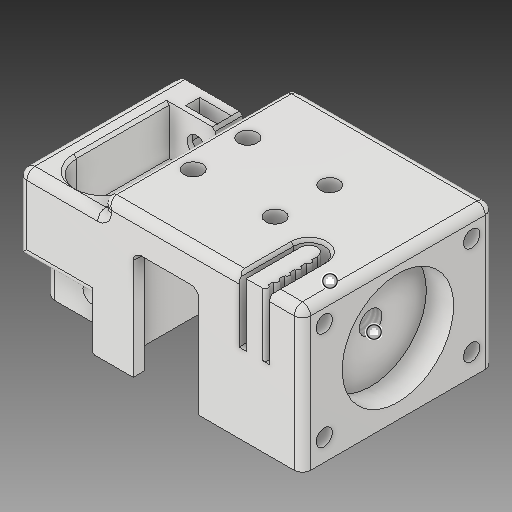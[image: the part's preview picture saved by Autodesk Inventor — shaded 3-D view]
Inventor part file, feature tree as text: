
AUTODESK INVENTOR PART (.ipt)
format: ipt  version: 2019 (Build 230136000, 136)  size: 547,840 bytes
history: native  units: mm
features: sketch x19, extrude x18, fillet x3, pattern_linear x2, plane x2, thicken_offset x2, mirror x1, chamfer x1, hole x1
ambient origin geometry x8: Origin, YZ Plane, XZ Plane, XY Plane, X Axis, Y Axis, Z Axis, Center Point
bodies: Solid1 (feature_tree)
feature tree (49):
  extrude  "Extrusion1"  Depth=15.0mm
  extrude  "Extrusion2"  Depth=20.0mm
  extrude  "Extrusion15"  Depth=15.0mm
  extrude  "Extrusion16"  Depth=10.0mm
  extrude  "Extrusion21"  Depth=10.0mm
  extrude  "Extrusion22"  Depth=10.0mm
  mirror  "Mirror12"
  extrude  "Extrusion23"  Depth=11.5mm TaperAngle=0.0deg
  pattern_linear  "Rectangular Pattern4"  Count1=5 Spacing1=2.0mm
  extrude  "Extrusion24"  Depth=3.0mm
  extrude  "Extrusion25"  Depth=10.0mm
  pattern_linear  "Rectangular Pattern5"  Spacing1=1.0mm  [1 undecoded]
  extrude  "Extrusion26"  Depth=10.0mm TaperAngle=0.0deg
  extrude  "Extrusion27"  Depth=2.0mm
  plane  "Work Plane6"
  extrude  "Extrusion28"  Depth=2.0mm
  thicken_offset  "Thicken1"
  extrude  "Extrusion29"  Depth=2.0mm
  extrude  "Extrusion30"  Depth=10.0mm
  extrude  "Extrusion31"  Depth=2.0mm
  plane  "Work Plane7"
  extrude  "Extrusion32"  Depth=2.0mm
  extrude  "Extrusion33"  Depth=2.0mm TaperAngle=0.0deg
  extrude  "Extrusion34"  Depth=2.0mm
  chamfer  "Chamfer5"  Distance=10.0mm
  thicken_offset  "Thicken2"
  fillet  "Fillet2"  [1 undecoded]
  fillet  "Fillet3"  Radius=2.6mm
  fillet  "Fillet4"  Radius=5.8mm
  hole  "Hole1"  [1 undecoded]
  sketch  "Sketch1"  dims[d0=3.0mm d1=15.0mm]
  sketch  "Sketch2"  dims[d2=20.0mm d4=23.0mm]
  sketch  "Sketch18"  dims[d5=35.0mm d6=0.0mm d7=15.0mm]
  sketch  "Sketch19"  dims[d8=10.0mm d9=3.4mm]
  sketch  "Sketch24"  dims[d10=10.0mm d11=0.0mm d106=1.3mm]
  sketch  "Sketch26"  dims[d107=10.0mm d108=3.0mm]
  sketch  "Sketch27"  dims[d110=3.4mm d111=11.5mm d112=0.0mm]
  sketch  "Sketch28"  dims[d113=13.5mm]
  sketch  "Sketch29"  dims[d114=6.0mm]
  sketch  "Sketch30"  dims[d115=12.0mm d116=0.0mm]
  sketch  "Sketch31"  dims[d140=3.0mm d141=0.0mm]
  sketch  "Sketch32"  dims[d142=12.0mm]
  sketch  "Sketch33"  dims[d143=3.0mm]
  sketch  "Sketch34"  dims[d144=2.0mm d145=0.0mm]
  sketch  "Sketch35"  dims[d146=1.0mm]
  sketch  "Sketch36"  dims[d147=2.0mm d148=0.0mm d149=50.0mm d151=2.0mm]
  sketch  "Sketch37"  dims[d152=1.3mm d153=3.0mm]
  sketch  "Sketch38"  dims[d154=10.0mm d155=3.3mm]
  sketch  "Sketch39"  dims[d156=9.0mm d157=0.0mm d158=1.0mm d159=10.0mm d160=0.0mm d161=50.0mm d163=2.0mm d164=1.6mm d166=5.0mm d167=10.0mm d168=1.9mm d169=7.0mm d170=5.25mm d171=0.0mm d172=3.4mm d173=10.0mm d174=0.0mm d175=-1.5mm d177=2.6mm d178=0.0mm d179=5.8mm d180=2.0mm d181=2.0mm d182=10.0mm d183=6.0mm d184=1.6mm d185=7.0mm d186=3.6mm d187=9.0mm d188=0.0mm d189=5.0mm d190=7.0mm d191=0.0mm d192=5.0mm d193=3.4mm d194=7.0mm d195=0.0mm d196=-1.5mm d197=5.7mm d198=3.0mm d199=0.0mm d202=4.0mm d203=4.0mm d204=3.0mm d205=5.0mm d206=0.0mm d209=5.0mm d210=0.0mm d212=0.5mm d213=2.0mm d214=45.0deg d215=6.0mm d216=6.0mm d217=1.0mm d218=1.5mm d219=1.5mm d220=20.4mm d221=4.134mm d222=10.0mm d223=4.0mm d224=2.0mm d225=90.0deg d226=14.2mm d227=20.594885mm d228=0.0mm d229=0.0mm]
note: 3 required parameter values undecoded (feature->parameter linkage not recoverable at this tier; creation-order binding heuristic only, values carry confidence <= 0.55)
